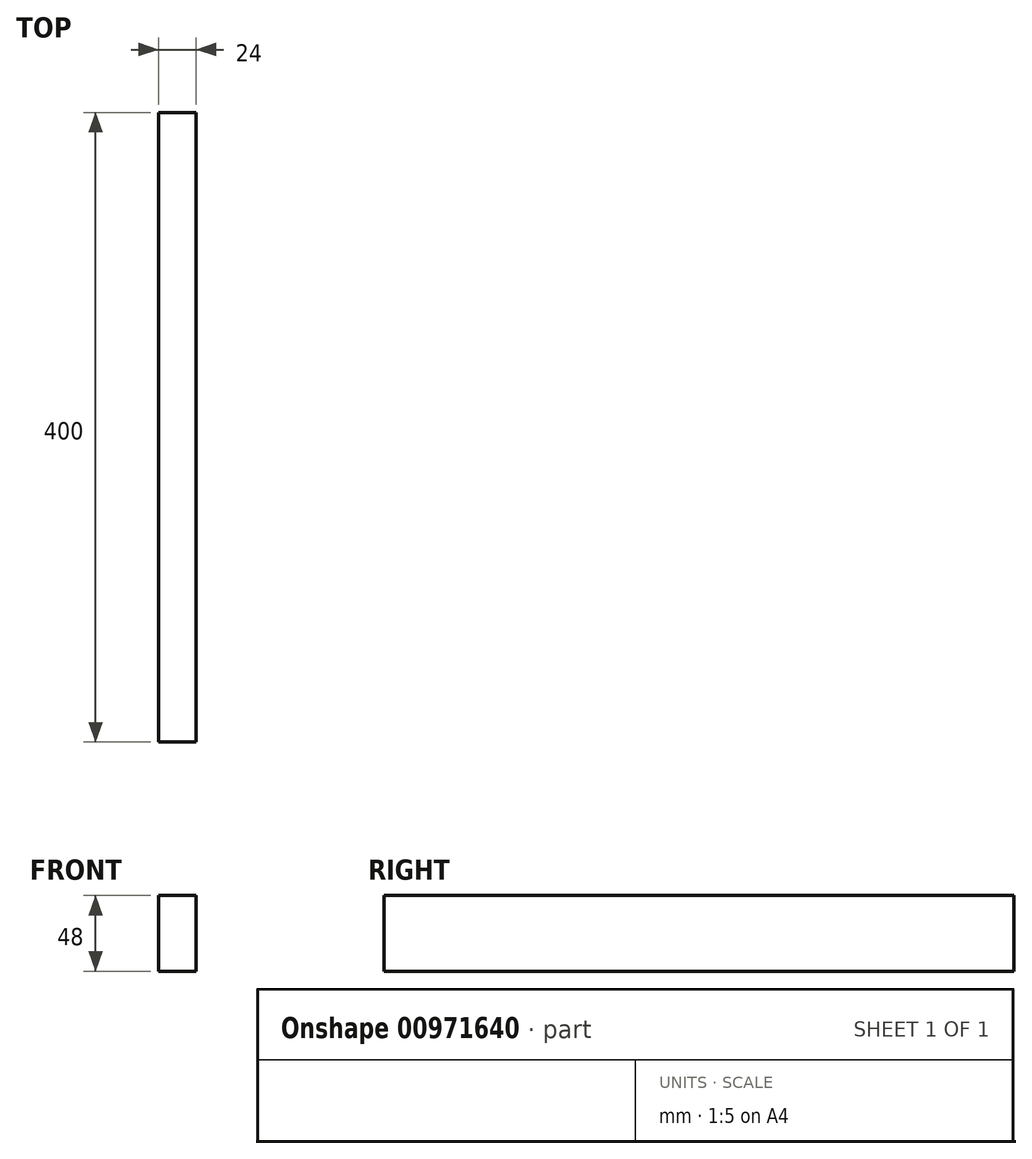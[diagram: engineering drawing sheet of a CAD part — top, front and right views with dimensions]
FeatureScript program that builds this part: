
annotation { "Feature Type Name" : "Feature", "Feature Type Description" : "" }
export const myFeature = defineFeature(function(context is Context, id is Id, definition is map)
    precondition{}
    {
        {
            assignVariable(context, id + "F0", {"name" : "c", "anyValue" : 400});
        }
        {
            var Q0;
            Q0=qCreatedBy(makeId("Front.planeOp"),FACE);
            var sketch = newSketch(context, id + "F1", { "sketchPlane" : qUnion([Q0])});
            skLineSegment(sketch, "E0.bottom", {"start": v(12, -24) * mm, "end": v(-12, -24) * mm});
            skLineSegment(sketch, "E0.top", {"start": v(12, 24) * mm, "end": v(-12, 24) * mm});
            skLineSegment(sketch, "E0.left", {"start": v(12, -24) * mm, "end": v(12, 24) * mm});
            skLineSegment(sketch, "E0.right", {"start": v(-12, -24) * mm, "end": v(-12, 24) * mm});
            skPoint(sketch, "E0.middle", {"position": v(0, 0) * mm});
            skSolve(sketch);
        }
        {
            var Q0;
            Q0=qSketchRegion(id+"F1",true);
            var Q1;
            Q1=makeQuery(id+"F1.imprint","IMPRINT",FACE,{"disambiguationData":[TD([[makeQuery(id+"F1.imprint","IMPRINT",EDGE,{"derivedFrom":sQuery(id+"F1.wireOp",EDGE,"E0.bottom")}),-1.0]])]});
            extrude(context, id + "F2", {"entities" : qUnion([Q0, Q1]), "depth" : (getVariable(context, 'c')) * mm, "offsetDistance" : 25 * mm});
        }
    });
